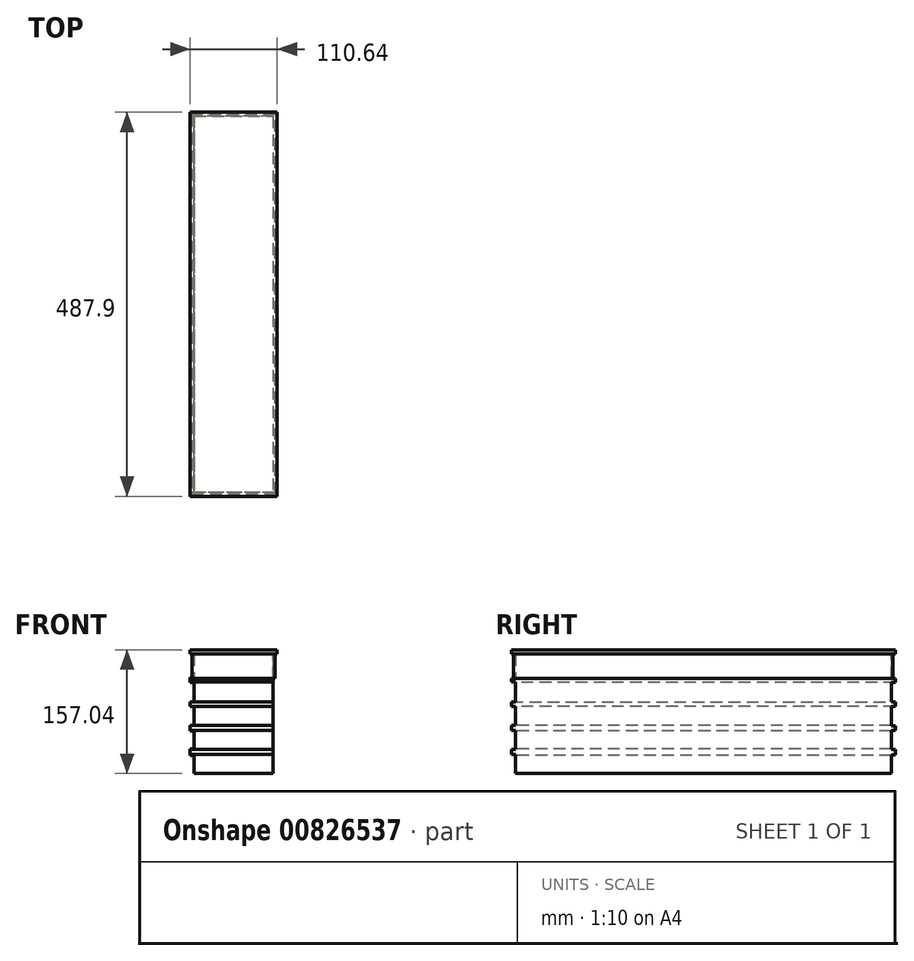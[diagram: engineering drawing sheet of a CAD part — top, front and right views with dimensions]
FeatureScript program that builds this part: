
annotation { "Feature Type Name" : "Feature", "Feature Type Description" : "" }
export const myFeature = defineFeature(function(context is Context, id is Id, definition is map)
    precondition{}
    {
        {
            var Q0;
            Q0=qCreatedBy(makeId("Front.planeOp"),FACE);
            var sketch = newSketch(context, id + "F0", { "sketchPlane" : qUnion([Q0])});
            skLineSegment(sketch, "E0.bottom", {"start": v(-55.2, 75.73) * mm, "end": v(55.2, 75.73) * mm});
            skLineSegment(sketch, "E0.top", {"start": v(-55.2, -75.73) * mm, "end": v(55.2, -75.73) * mm});
            skLineSegment(sketch, "E0.left", {"start": v(-55.2, 75.73) * mm, "end": v(-55.2, -75.73) * mm});
            skLineSegment(sketch, "E0.right", {"start": v(55.2, 75.73) * mm, "end": v(55.2, -75.73) * mm});
            skPoint(sketch, "E0.middle", {"position": v(0, 0) * mm});
            skSolve(sketch);
        }
        {
            var Q0;
            Q0 = qSketchRegion(id + "F0", true);
            extrude(context, id + "F1", {"entities" : qUnion([Q0]), "oppositeDirection" : true, "depth" : 487.68 * mm, "offsetDistance" : 25.4 * mm});
        }
        {
            var Q0;
            Q0=makeQuery(id+"F1.opExtrude","SWEPT_FACE",FACE,{"disambiguationData":[OSD([sQuery(id+"F0.wireOp",EDGE,"E0.right")])]});
            var sketch = newSketch(context, id + "F2", { "sketchPlane" : qUnion([Q0])});
            skLineSegment(sketch, "E1", {"start": v(487.68, 75.73) * mm, "end": v(487.68, -75.73) * mm});
            skLineSegment(sketch, "E2", {"start": v(487.68, -75.73) * mm, "end": v(487.68, -45.5) * mm});
            skLineSegment(sketch, "E3", {"start": v(487.68, -45.5) * mm, "end": v(487.68, -15.27) * mm});
            skLineSegment(sketch, "E4", {"start": v(487.68, -15.27) * mm, "end": v(487.68, 14.95) * mm});
            skLineSegment(sketch, "E5", {"start": v(487.68, 14.95) * mm, "end": v(487.68, 45.18) * mm});
            skLineSegment(sketch, "E6", {"start": v(487.68, 45.18) * mm, "end": v(487.68, 75.4) * mm});
            skLineSegment(sketch, "E7", {"start": v(487.68, -45.5) * mm, "end": v(0, -45.5) * mm});
            skLineSegment(sketch, "E8", {"start": v(487.68, -15.27) * mm, "end": v(0, -15.27) * mm});
            skLineSegment(sketch, "E9", {"start": v(487.68, 14.95) * mm, "end": v(0, 14.95) * mm});
            skLineSegment(sketch, "E10", {"start": v(487.68, 45.18) * mm, "end": v(0, 45.18) * mm});
            skLineSegment(sketch, "E11", {"start": v(0, 39.75) * mm, "end": v(487.68, 39.75) * mm});
            skLineSegment(sketch, "E12", {"start": v(0, 9.08) * mm, "end": v(487.68, 9.08) * mm});
            skLineSegment(sketch, "E13", {"start": v(0, -21.37) * mm, "end": v(487.68, -21.37) * mm});
            skLineSegment(sketch, "E14", {"start": v(0, -52.23) * mm, "end": v(487.68, -52.23) * mm});
            skSolve(sketch);
        }
        {
            var Q0;
            Q0=makeQuery(id+"F1.opExtrude","CAP_FACE",FACE,{"disambiguationData":[OSD([sQuery(id+"F0.wireOp",EDGE,"E0.bottom"),sQuery(id+"F0.wireOp",EDGE,"E0.top"),sQuery(id+"F0.wireOp",EDGE,"E0.left"),sQuery(id+"F0.wireOp",EDGE,"E0.right")])],"isStart":false});
            var sketch = newSketch(context, id + "F3", { "sketchPlane" : qUnion([Q0])});
            skLineSegment(sketch, "E15", {"start": v(-55.2, 44.9) * mm, "end": v(55.2, 44.9) * mm});
            skLineSegment(sketch, "E16", {"start": v(-55.2, 39.7) * mm, "end": v(55.2, 39.7) * mm});
            skLineSegment(sketch, "E17", {"start": v(-55.2, 15.06) * mm, "end": v(55.2, 15.06) * mm});
            skLineSegment(sketch, "E18", {"start": v(-55.2, 9.1) * mm, "end": v(55.2, 9.1) * mm});
            skLineSegment(sketch, "E19", {"start": v(-55.2, -15.27) * mm, "end": v(55.2, -15.27) * mm});
            skLineSegment(sketch, "E20", {"start": v(-55.2, -21.25) * mm, "end": v(55.2, -21.25) * mm});
            skLineSegment(sketch, "E21", {"start": v(-55.2, -45.23) * mm, "end": v(55.2, -45.23) * mm});
            skLineSegment(sketch, "E22", {"start": v(-55.2, -52.18) * mm, "end": v(55.2, -52.18) * mm});
            skSolve(sketch);
        }
        {
            var Q0;
            Q0=makeQuery(id+"F1.opExtrude","SWEPT_FACE",FACE,{"disambiguationData":[OSD([sQuery(id+"F0.wireOp",EDGE,"E0.left")])]});
            var sketch = newSketch(context, id + "F4", { "sketchPlane" : qUnion([Q0])});
            skLineSegment(sketch, "E23", {"start": v(-487.68, 9.27) * mm, "end": v(0, 9.27) * mm});
            skLineSegment(sketch, "E24", {"start": v(0, 15.27) * mm, "end": v(-487.68, 15.27) * mm});
            skLineSegment(sketch, "E25", {"start": v(-487.68, 40.05) * mm, "end": v(0, 40.05) * mm});
            skLineSegment(sketch, "E26", {"start": v(0, 45.86) * mm, "end": v(-487.68, 45.86) * mm});
            skLineSegment(sketch, "E27", {"start": v(-487.68, -14.51) * mm, "end": v(0, -14.51) * mm});
            skLineSegment(sketch, "E28", {"start": v(-487.68, -22.06) * mm, "end": v(0, -22.06) * mm});
            skLineSegment(sketch, "E29", {"start": v(-487.68, -44.7) * mm, "end": v(0, -44.7) * mm});
            skLineSegment(sketch, "E30", {"start": v(-487.68, -52.82) * mm, "end": v(0, -52.82) * mm});
            skSolve(sketch);
        }
        {
            var Q0;
            Q0=makeQuery(id+"F1.opExtrude","CAP_FACE",FACE,{"disambiguationData":[OSD([sQuery(id+"F0.wireOp",EDGE,"E0.bottom"),sQuery(id+"F0.wireOp",EDGE,"E0.top"),sQuery(id+"F0.wireOp",EDGE,"E0.left"),sQuery(id+"F0.wireOp",EDGE,"E0.right")])],"isStart":true});
            var sketch = newSketch(context, id + "F5", { "sketchPlane" : qUnion([Q0])});
            skLineSegment(sketch, "E31", {"start": v(-55.2, 45.06) * mm, "end": v(55.2, 45.06) * mm});
            skLineSegment(sketch, "E32", {"start": v(55.2, 40.19) * mm, "end": v(-55.2, 40.19) * mm});
            skLineSegment(sketch, "E33", {"start": v(-55.2, 15.34) * mm, "end": v(55.2, 15.34) * mm});
            skLineSegment(sketch, "E34", {"start": v(55.2, 9.26) * mm, "end": v(-55.2, 9.26) * mm});
            skLineSegment(sketch, "E35", {"start": v(-55.2, -15.1) * mm, "end": v(55.2, -15.1) * mm});
            skLineSegment(sketch, "E36", {"start": v(-55.2, -20.95) * mm, "end": v(55.2, -20.95) * mm});
            skLineSegment(sketch, "E37", {"start": v(-55.2, -45.06) * mm, "end": v(55.2, -45.06) * mm});
            skLineSegment(sketch, "E38", {"start": v(-55.2, -51.88) * mm, "end": v(55.2, -51.88) * mm});
            skSolve(sketch);
        }
        {
            var Q0;
            {var subQ0=sQuery(id+"F2.wireOp",EDGE,"E9");Q0=makeQuery(id+"F2.imprint","IMPRINT",FACE,{"disambiguationData":[TD([[makeQuery(id+"F2.imprint","IMPRINT",EDGE,{"derivedFrom":subQ0}),-1.0]])]});}
            var Q1;
            {var subQ3=sQuery(id+"F2.wireOp",EDGE,"E14");Q1=makeQuery(id+"F2.imprint","IMPRINT",FACE,{"disambiguationData":[TD([[makeQuery(id+"F2.imprint","IMPRINT",EDGE,{"derivedFrom":subQ3}),-1.0]])]});}
            var Q2;
            {var subQ0=sQuery(id+"F2.wireOp",EDGE,"E7");Q2=makeQuery(id+"F2.imprint","IMPRINT",FACE,{"disambiguationData":[TD([[makeQuery(id+"F2.imprint","IMPRINT",EDGE,{"derivedFrom":subQ0}),-1.0]])]});}
            var Q3;
            {var subQ0=sQuery(id+"F2.wireOp",EDGE,"E8");Q3=makeQuery(id+"F2.imprint","IMPRINT",FACE,{"disambiguationData":[TD([[makeQuery(id+"F2.imprint","IMPRINT",EDGE,{"derivedFrom":subQ0}),-1.0]])]});}
            var Q4;
            Q4=makeQuery(id+"F2.imprint","IMPRINT",FACE,{"disambiguationData":[TD([[makeQuery(id+"F2.imprint","IMPRINT",EDGE,{"derivedFrom":sQuery(id+"F2.wireOp",EDGE,"E1")}),-1.0]])]});
            extrude(context, id + "F6", {"entities" : qUnion([Q0, Q1, Q2, Q3, Q4]), "operationType" : NewBodyOperationType.REMOVE, "oppositeDirection" : true, "depth" : 5.08 * mm, "offsetDistance" : 25.4 * mm});
        }
        {
            var Q0;
            {var subQ0=sQuery(id+"F5.wireOp",EDGE,"E38");Q0=makeQuery(id+"F5.imprint","IMPRINT",FACE,{"disambiguationData":[TD([[makeQuery(id+"F5.imprint","IMPRINT",EDGE,{"derivedFrom":subQ0}),-1.0]])]});}
            var Q1;
            {var subQ0=sQuery(id+"F5.wireOp",EDGE,"E36");Q1=makeQuery(id+"F5.imprint","IMPRINT",FACE,{"disambiguationData":[TD([[makeQuery(id+"F5.imprint","IMPRINT",EDGE,{"derivedFrom":subQ0}),-1.0]])]});}
            var Q2;
            {var subQ0=sQuery(id+"F5.wireOp",EDGE,"E34");Q2=makeQuery(id+"F5.imprint","IMPRINT",FACE,{"disambiguationData":[TD([[makeQuery(id+"F5.imprint","IMPRINT",EDGE,{"derivedFrom":subQ0}),1.0]])]});}
            var Q3;
            {var subQ0=sQuery(id+"F5.wireOp",EDGE,"E32");Q3=makeQuery(id+"F5.imprint","IMPRINT",FACE,{"disambiguationData":[TD([[makeQuery(id+"F5.imprint","IMPRINT",EDGE,{"derivedFrom":subQ0}),1.0]])]});}
            var Q4;
            {var subQ0=sQuery(id+"F5.wireOp",EDGE,"E31");Q4=makeQuery(id+"F5.imprint","IMPRINT",FACE,{"disambiguationData":[TD([[makeQuery(id+"F5.imprint","IMPRINT",EDGE,{"derivedFrom":subQ0}),1.0]])]});}
            extrude(context, id + "F7", {"entities" : qUnion([Q0, Q1, Q2, Q3, Q4]), "operationType" : NewBodyOperationType.REMOVE, "oppositeDirection" : true, "depth" : 5.08 * mm, "offsetDistance" : 25.4 * mm});
        }
        {
            var Q0;
            {var subQ0=sQuery(id+"F4.wireOp",EDGE,"E23");Q0=makeQuery(id+"F4.imprint","IMPRINT",FACE,{"disambiguationData":[TD([[makeQuery(id+"F4.imprint","IMPRINT",EDGE,{"derivedFrom":subQ0}),-1.0]])]});}
            var Q1;
            {var subQ0=sQuery(id+"F4.wireOp",EDGE,"E28");Q1=makeQuery(id+"F4.imprint","IMPRINT",FACE,{"disambiguationData":[TD([[makeQuery(id+"F4.imprint","IMPRINT",EDGE,{"derivedFrom":subQ0}),-1.0]])]});}
            var Q2;
            {var subQ0=sQuery(id+"F4.wireOp",EDGE,"E30");Q2=makeQuery(id+"F4.imprint","IMPRINT",FACE,{"disambiguationData":[TD([[makeQuery(id+"F4.imprint","IMPRINT",EDGE,{"derivedFrom":subQ0}),-1.0]])]});}
            var Q3;
            {var subQ0=sQuery(id+"F4.wireOp",EDGE,"E24");Q3=makeQuery(id+"F4.imprint","IMPRINT",FACE,{"disambiguationData":[TD([[makeQuery(id+"F4.imprint","IMPRINT",EDGE,{"derivedFrom":subQ0}),-1.0]])]});}
            var Q4;
            {var subQ0=sQuery(id+"F4.wireOp",EDGE,"E26");Q4=makeQuery(id+"F4.imprint","IMPRINT",FACE,{"disambiguationData":[TD([[makeQuery(id+"F4.imprint","IMPRINT",EDGE,{"derivedFrom":subQ0}),-1.0]])]});}
            extrude(context, id + "F8", {"entities" : qUnion([Q0, Q1, Q2, Q3, Q4]), "operationType" : NewBodyOperationType.REMOVE, "oppositeDirection" : true, "depth" : 5.08 * mm, "offsetDistance" : 25.4 * mm});
        }
        {
            var Q0;
            {var subQ0=sQuery(id+"F3.wireOp",EDGE,"E16");Q0=makeQuery(id+"F3.imprint","IMPRINT",FACE,{"disambiguationData":[TD([[makeQuery(id+"F3.imprint","IMPRINT",EDGE,{"derivedFrom":subQ0}),-1.0]])]});}
            var Q1;
            {var subQ0=sQuery(id+"F3.wireOp",EDGE,"E15");Q1=makeQuery(id+"F3.imprint","IMPRINT",FACE,{"disambiguationData":[TD([[makeQuery(id+"F3.imprint","IMPRINT",EDGE,{"derivedFrom":subQ0}),1.0]])]});}
            var Q2;
            {var subQ0=sQuery(id+"F3.wireOp",EDGE,"E18");Q2=makeQuery(id+"F3.imprint","IMPRINT",FACE,{"disambiguationData":[TD([[makeQuery(id+"F3.imprint","IMPRINT",EDGE,{"derivedFrom":subQ0}),-1.0]])]});}
            var Q3;
            {var subQ0=sQuery(id+"F3.wireOp",EDGE,"E20");Q3=makeQuery(id+"F3.imprint","IMPRINT",FACE,{"disambiguationData":[TD([[makeQuery(id+"F3.imprint","IMPRINT",EDGE,{"derivedFrom":subQ0}),-1.0]])]});}
            var Q4;
            {var subQ0=sQuery(id+"F3.wireOp",EDGE,"E22");Q4=makeQuery(id+"F3.imprint","IMPRINT",FACE,{"disambiguationData":[TD([[makeQuery(id+"F3.imprint","IMPRINT",EDGE,{"derivedFrom":subQ0}),-1.0]])]});}
            extrude(context, id + "F9", {"entities" : qUnion([Q0, Q1, Q2, Q3, Q4]), "operationType" : NewBodyOperationType.REMOVE, "oppositeDirection" : true, "depth" : 5.08 * mm, "offsetDistance" : 25.4 * mm});
        }
        {
            var Q0;
            Q0=makeQuery(id+"F1.opExtrude","SWEPT_FACE",FACE,{"disambiguationData":[OSD([sQuery(id+"F0.wireOp",EDGE,"E0.bottom")])]});
            var sketch = newSketch(context, id + "F10", { "sketchPlane" : qUnion([Q0])});
            skLineSegment(sketch, "E39.bottom", {"start": v(-55.32, 487.79) * mm, "end": v(55.32, 487.79) * mm});
            skLineSegment(sketch, "E39.top", {"start": v(-55.32, -0.1) * mm, "end": v(55.32, -0.1) * mm});
            skLineSegment(sketch, "E39.left", {"start": v(-55.32, 487.79) * mm, "end": v(-55.32, -0.1) * mm});
            skLineSegment(sketch, "E39.right", {"start": v(55.32, 487.79) * mm, "end": v(55.32, -0.1) * mm});
            skPoint(sketch, "E39.middle", {"position": v(0, 243.84) * mm});
            skSolve(sketch);
        }
        {
            var Q0;
            Q0 = qSketchRegion(id + "F10", true);
            extrude(context, id + "F11", {"entities" : qUnion([Q0]), "depth" : 5.6 * mm, "offsetDistance" : 25.4 * mm});
        }
        {
            var Q0;
            Q0=makeQuery(id+"F7.boolean.opBoolean","COPY",FACE,{"derivedFrom":makeQuery(id+"F7.opExtrude","SWEPT_FACE",FACE,{"disambiguationData":[OSD([sQuery(id+"F5.wireOp",EDGE,"E31")])]})});
            var sketch = newSketch(context, id + "F12", { "sketchPlane" : qUnion([Q0])});
            skLineSegment(sketch, "E40", {"start": v(-52.92, 2.87) * mm, "end": v(52.85, 2.87) * mm});
            skLineSegment(sketch, "E41", {"start": v(52.85, 2.87) * mm, "end": v(52.85, 484.76) * mm});
            skLineSegment(sketch, "E42", {"start": v(52.85, 484.76) * mm, "end": v(-52.72, 484.76) * mm});
            skLineSegment(sketch, "E43", {"start": v(-52.72, 484.76) * mm, "end": v(-52.92, 2.87) * mm});
            skSolve(sketch);
        }
        {
            var Q0;
            Q0 = qSketchRegion(id + "F12", true);
            extrude(context, id + "F13", {"entities" : qUnion([Q0]), "depth" : 31.75 * mm, "offsetDistance" : 25.4 * mm});
        }
    });
